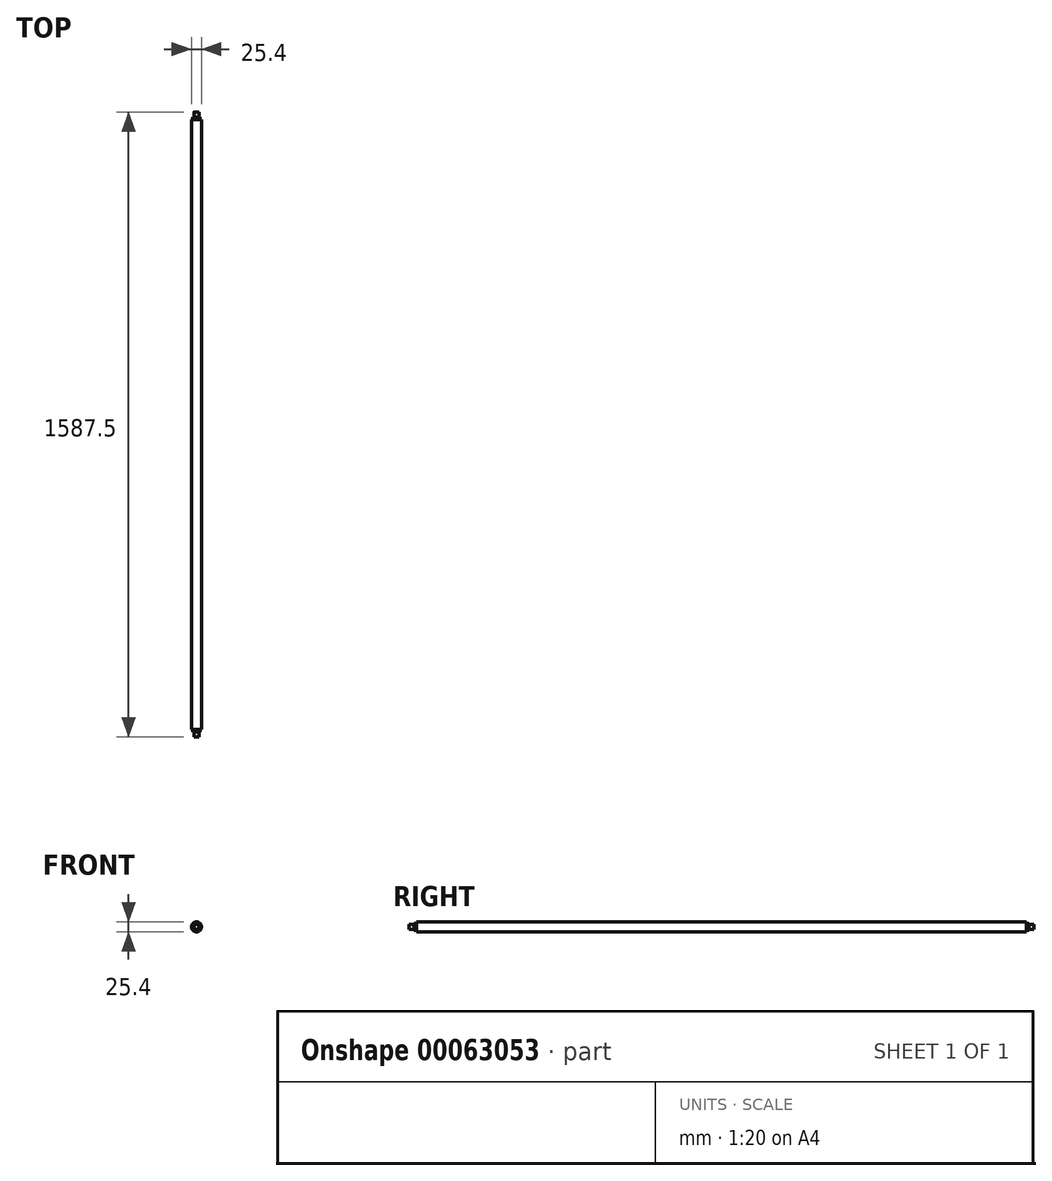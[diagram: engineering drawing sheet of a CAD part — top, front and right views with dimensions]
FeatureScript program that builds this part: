
annotation { "Feature Type Name" : "Feature", "Feature Type Description" : "" }
export const myFeature = defineFeature(function(context is Context, id is Id, definition is map)
    precondition{}
    {
        {
            var Q0;
            Q0=qCreatedBy(makeId("Front.planeOp"),FACE);
            var sketch = newSketch(context, id + "F0", { "sketchPlane" : qUnion([Q0])});
            skCircle(sketch, "E0", {"center": v(0, 0) * mm, "radius": 12.7 * mm});
            skSolve(sketch);
        }
        {
            var Q0;
            Q0=makeQuery(id+"F0.imprint","IMPRINT",FACE,{"disambiguationData":[TD([[makeQuery(id+"F0.imprint","IMPRINT",EDGE,{"derivedFrom":sQuery(id+"F0.wireOp",EDGE,"E0")}),1.0]])]});
            extrude(context, id + "F1", {"entities" : qUnion([Q0]), "endBound" : BoundingType.SYMMETRIC, "depth" : 1587.5 * mm});
        }
        {
            var Q0;
            Q0=makeQuery(id+"F1.opExtrude","CAP_FACE",FACE,{"disambiguationData":[OSD([sQuery(id+"F0.wireOp",EDGE,"E0")])],"isStart":false});
            var sketch = newSketch(context, id + "F2", { "sketchPlane" : qUnion([Q0])});
            skCircle(sketch, "E1", {"center": v(0, 0) * mm, "radius": 12.7 * mm});
            skCircle(sketch, "E2", {"center": v(0, 0) * mm, "radius": 9.4 * mm});
            skSolve(sketch);
        }
        {
            var Q0;
            Q0=makeQuery(id+"F2.imprint","IMPRINT",FACE,{"disambiguationData":[TD([[makeQuery(id+"F2.imprint","IMPRINT",EDGE,{"derivedFrom":sQuery(id+"F2.wireOp",EDGE,"E1")}),1.0]])]});
            extrude(context, id + "F3", {"entities" : qUnion([Q0]), "operationType" : NewBodyOperationType.REMOVE, "oppositeDirection" : true, "depth" : 19.05 * mm});
        }
        {
            var Q0;
            Q0=makeQuery(id+"F1.opExtrude","CAP_FACE",FACE,{"disambiguationData":[OSD([sQuery(id+"F0.wireOp",EDGE,"E0")])],"isStart":true});
            var sketch = newSketch(context, id + "F4", { "sketchPlane" : qUnion([Q0])});
            skCircle(sketch, "E3", {"center": v(0, 0) * mm, "radius": 9.4 * mm});
            skCircle(sketch, "E4", {"center": v(0, 0) * mm, "radius": 12.7 * mm});
            skSolve(sketch);
        }
        {
            var Q0;
            Q0 = qSketchRegion(id + "F4", true);
            extrude(context, id + "F5", {"entities" : qUnion([Q0]), "operationType" : NewBodyOperationType.REMOVE, "oppositeDirection" : true, "depth" : 19.05 * mm});
        }
        {
            var Q0;
            Q0=makeQuery(id+"F1.opExtrude","CAP_FACE",FACE,{"disambiguationData":[OSD([sQuery(id+"F0.wireOp",EDGE,"E0")])],"isStart":false});
            var sketch = newSketch(context, id + "F6", { "sketchPlane" : qUnion([Q0])});
            skCircle(sketch, "E5", {"center": v(0, 0) * mm, "radius": 6.35 * mm});
            skCircle(sketch, "E6", {"center": v(0, 0) * mm, "radius": 9.4 * mm});
            skSolve(sketch);
        }
        {
            var Q0;
            Q0=makeQuery(id+"F6.imprint","IMPRINT",FACE,{"disambiguationData":[TD([[makeQuery(id+"F6.imprint","IMPRINT",EDGE,{"derivedFrom":sQuery(id+"F6.wireOp",EDGE,"E5")}),-1.0]])]});
            extrude(context, id + "F7", {"entities" : qUnion([Q0]), "operationType" : NewBodyOperationType.REMOVE, "oppositeDirection" : true, "depth" : 12.7 * mm});
        }
        {
            var Q0;
            Q0=makeQuery(id+"F1.opExtrude","CAP_FACE",FACE,{"disambiguationData":[OSD([sQuery(id+"F0.wireOp",EDGE,"E0")])],"isStart":true});
            var sketch = newSketch(context, id + "F8", { "sketchPlane" : qUnion([Q0])});
            skCircle(sketch, "E7", {"center": v(0, 0) * mm, "radius": 6.35 * mm});
            skCircle(sketch, "E8", {"center": v(0, 0) * mm, "radius": 9.4 * mm});
            skSolve(sketch);
        }
        {
            var Q0;
            Q0=makeQuery(id+"F8.imprint","IMPRINT",FACE,{"disambiguationData":[TD([[makeQuery(id+"F8.imprint","IMPRINT",EDGE,{"derivedFrom":sQuery(id+"F8.wireOp",EDGE,"E7")}),-1.0]])]});
            extrude(context, id + "F9", {"entities" : qUnion([Q0]), "operationType" : NewBodyOperationType.REMOVE, "oppositeDirection" : true, "depth" : 12.7 * mm});
        }
    });
